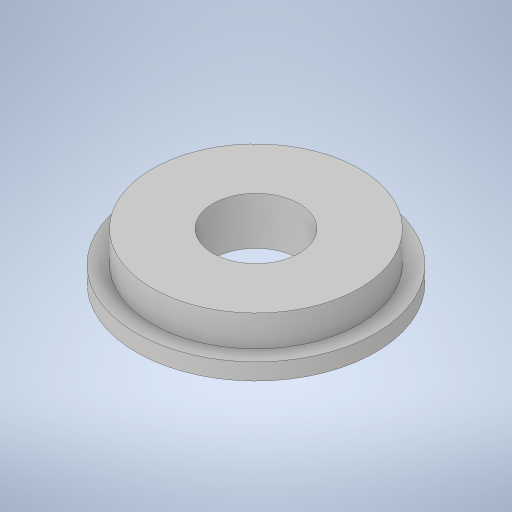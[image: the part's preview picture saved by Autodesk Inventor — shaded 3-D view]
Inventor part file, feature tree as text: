
AUTODESK INVENTOR PART (.ipt)
format: ipt  version: 2023.3 (Build 273359000, 359)  size: 243,200 bytes
history: native  units: in
note: dims shown in document units (in); Inventor stores cm internally (conversion verified against a paired STEP export)
features: sketch x3, extrude x2, hole x1
ambient origin geometry x8: Origin, YZ Plane, XZ Plane, XY Plane, X Axis, Y Axis, Z Axis, Center Point
bodies: Solid1 (feature_tree)
feature tree (6):
  extrude  "Extrusion1"  Depth=0.235in TaperAngle=0.0deg
  extrude  "Extrusion2"  Depth=0.175in TaperAngle=0.0deg
  hole  "Hole1"  [1 undecoded]
  sketch  "Sketch1"  dims[d0=0.865in d1=0.235in d2=0.0in]
  sketch  "Sketch2"  dims[d3=0.75in d4=0.175in d5=0.0in]
  sketch  "Sketch3"  dims[d6=0.3125in d7=0.75in d8=0.969in d9=0.0625in d10=0.5635in d11=1.0in d12=0.8108in]
note: 1 required parameter value undecoded (feature->parameter linkage not recoverable at this tier; creation-order binding heuristic only, values carry confidence <= 0.55)
